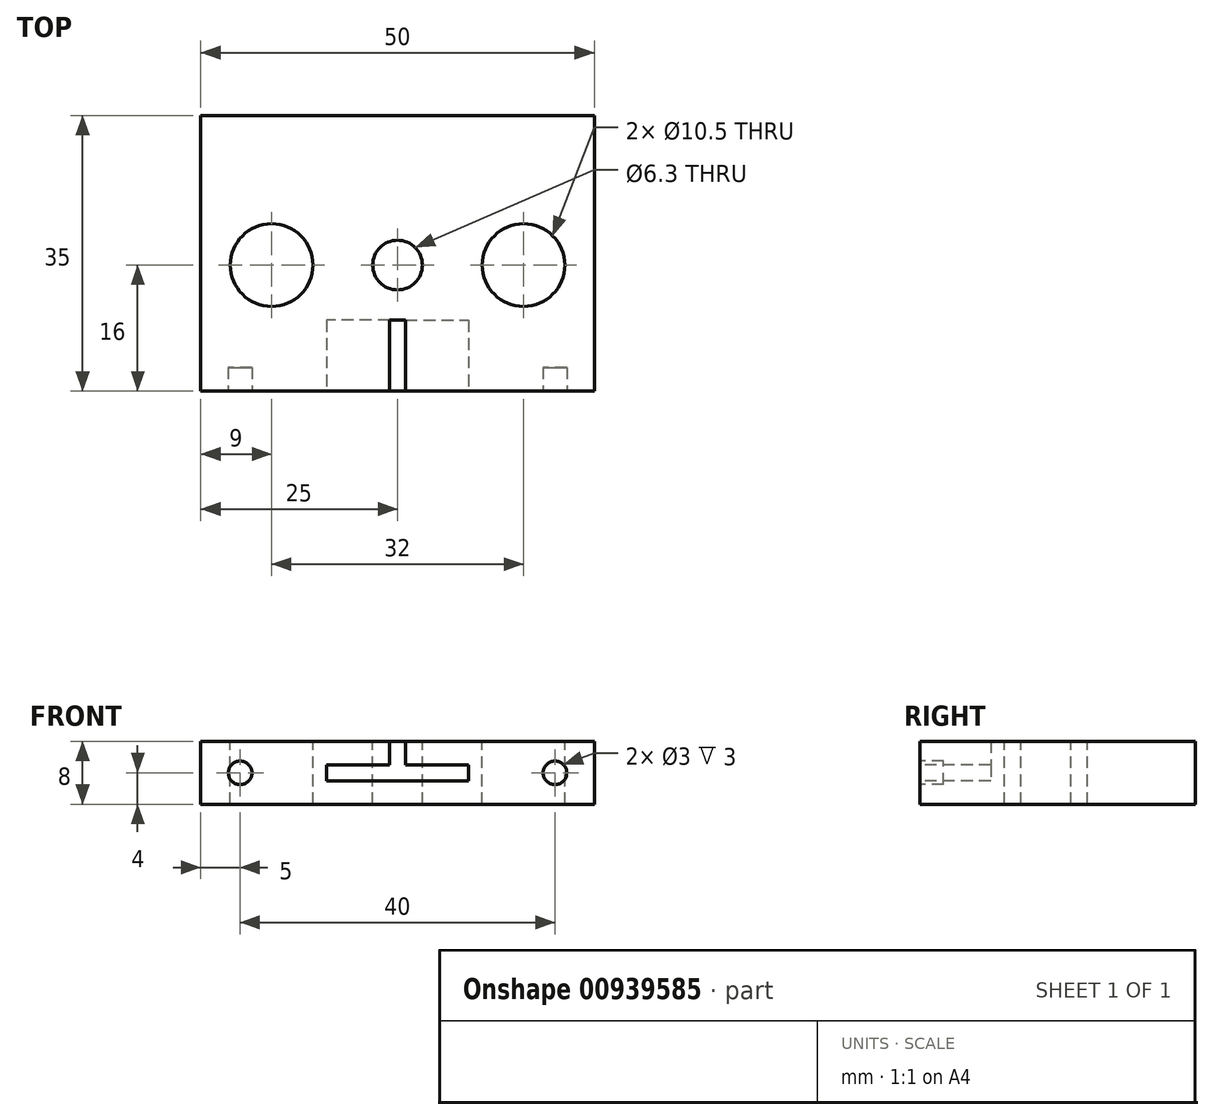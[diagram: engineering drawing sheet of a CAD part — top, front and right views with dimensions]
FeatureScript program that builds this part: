
annotation { "Feature Type Name" : "Feature", "Feature Type Description" : "" }
export const myFeature = defineFeature(function(context is Context, id is Id, definition is map)
    precondition{}
    {
        {
            var Q0;
            Q0=qCreatedBy(makeId("Top.planeOp"),FACE);
            var sketch = newSketch(context, id + "F0", { "sketchPlane" : qUnion([Q0])});
            skLineSegment(sketch, "E0.bottom", {"start": v(0, 0) * mm, "end": v(50, 0) * mm});
            skLineSegment(sketch, "E0.top", {"start": v(0, 35) * mm, "end": v(50, 35) * mm});
            skLineSegment(sketch, "E0.left", {"start": v(0, 0) * mm, "end": v(0, 35) * mm});
            skLineSegment(sketch, "E0.right", {"start": v(50, 0) * mm, "end": v(50, 35) * mm});
            skSolve(sketch);
        }
        {
            var Q0;
            Q0=makeQuery(id+"F0.imprint","IMPRINT",FACE,{"disambiguationData":[TD([[makeQuery(id+"F0.imprint","IMPRINT",EDGE,{"derivedFrom":sQuery(id+"F0.wireOp",EDGE,"E0.bottom")}),1.0]])]});
            extrude(context, id + "F1", {"entities" : qUnion([Q0]), "depth" : 8 * mm, "offsetDistance" : 25 * mm});
        }
        {
            var Q0;
            Q0=makeQuery(id+"F1.opExtrude","CAP_FACE",FACE,{"disambiguationData":[OSD([sQuery(id+"F0.wireOp",EDGE,"E0.bottom"),sQuery(id+"F0.wireOp",EDGE,"E0.top"),sQuery(id+"F0.wireOp",EDGE,"E0.left"),sQuery(id+"F0.wireOp",EDGE,"E0.right")])],"isStart":false});
            var sketch = newSketch(context, id + "F2", { "sketchPlane" : qUnion([Q0])});
            skCircle(sketch, "E1", {"center": v(41, 16) * mm, "radius": 5.25 * mm});
            skCircle(sketch, "E2", {"center": v(9, 16) * mm, "radius": 5.25 * mm});
            skCircle(sketch, "E3", {"center": v(25, 16) * mm, "radius": 3.15 * mm});
            skSolve(sketch);
        }
        {
            var Q0;
            Q0=makeQuery(id+"F2.imprint","IMPRINT",FACE,{"disambiguationData":[TD([[makeQuery(id+"F2.imprint","IMPRINT",EDGE,{"derivedFrom":sQuery(id+"F2.wireOp",EDGE,"E2")}),1.0]])]});
            var Q1;
            Q1=makeQuery(id+"F2.imprint","IMPRINT",FACE,{"disambiguationData":[TD([[makeQuery(id+"F2.imprint","IMPRINT",EDGE,{"derivedFrom":sQuery(id+"F2.wireOp",EDGE,"E1")}),1.0]])]});
            var Q2;
            Q2=makeQuery(id+"F2.imprint","IMPRINT",FACE,{"disambiguationData":[TD([[makeQuery(id+"F2.imprint","IMPRINT",EDGE,{"derivedFrom":sQuery(id+"F2.wireOp",EDGE,"E3")}),1.0]])]});
            extrude(context, id + "F3", {"entities" : qUnion([Q0, Q1, Q2]), "operationType" : NewBodyOperationType.REMOVE, "oppositeDirection" : true, "depth" : 8 * mm, "offsetDistance" : 25 * mm});
        }
        {
            var Q0;
            Q0=makeQuery(id+"F1.opExtrude","SWEPT_FACE",FACE,{"disambiguationData":[OSD([sQuery(id+"F0.wireOp",EDGE,"E0.bottom")])]});
            var sketch = newSketch(context, id + "F4", { "sketchPlane" : qUnion([Q0])});
            skCircle(sketch, "E4", {"center": v(5, 4) * mm, "radius": 1.5 * mm});
            skCircle(sketch, "E5", {"center": v(45, 4) * mm, "radius": 1.5 * mm});
            skLineSegment(sketch, "E6", {"start": v(24, 8) * mm, "end": v(24, 5) * mm});
            skLineSegment(sketch, "E7", {"start": v(24, 5) * mm, "end": v(16, 5) * mm});
            skLineSegment(sketch, "E8", {"start": v(16, 5) * mm, "end": v(16, 3) * mm});
            skLineSegment(sketch, "E9", {"start": v(16, 3) * mm, "end": v(34, 3) * mm});
            skLineSegment(sketch, "E10", {"start": v(34, 3) * mm, "end": v(34, 5) * mm});
            skLineSegment(sketch, "E11", {"start": v(34, 5) * mm, "end": v(26, 5) * mm});
            skLineSegment(sketch, "E12", {"start": v(26, 5) * mm, "end": v(26, 8) * mm});
            skSolve(sketch);
        }
        {
            var Q0;
            Q0=makeQuery(id+"F4.imprint","IMPRINT",FACE,{"disambiguationData":[TD([[makeQuery(id+"F4.imprint","IMPRINT",EDGE,{"derivedFrom":sQuery(id+"F4.wireOp",EDGE,"E4")}),1.0]])]});
            var Q1;
            Q1=makeQuery(id+"F4.imprint","IMPRINT",FACE,{"disambiguationData":[TD([[makeQuery(id+"F4.imprint","IMPRINT",EDGE,{"derivedFrom":sQuery(id+"F4.wireOp",EDGE,"E5")}),1.0]])]});
            extrude(context, id + "F5", {"entities" : qUnion([Q0, Q1]), "operationType" : NewBodyOperationType.REMOVE, "oppositeDirection" : true, "depth" : 3 * mm, "offsetDistance" : 25 * mm});
        }
        {
            var Q0;
            {var subQ0=sQuery(id+"F4.wireOp",EDGE,"E6");Q0=makeQuery(id+"F4.imprint","IMPRINT",FACE,{"disambiguationData":[TD([[makeQuery(id+"F4.imprint","IMPRINT",EDGE,{"derivedFrom":subQ0}),1.0]])]});}
            extrude(context, id + "F6", {"entities" : qUnion([Q0]), "operationType" : NewBodyOperationType.REMOVE, "oppositeDirection" : true, "depth" : 9 * mm, "offsetDistance" : 25 * mm});
        }
    });
